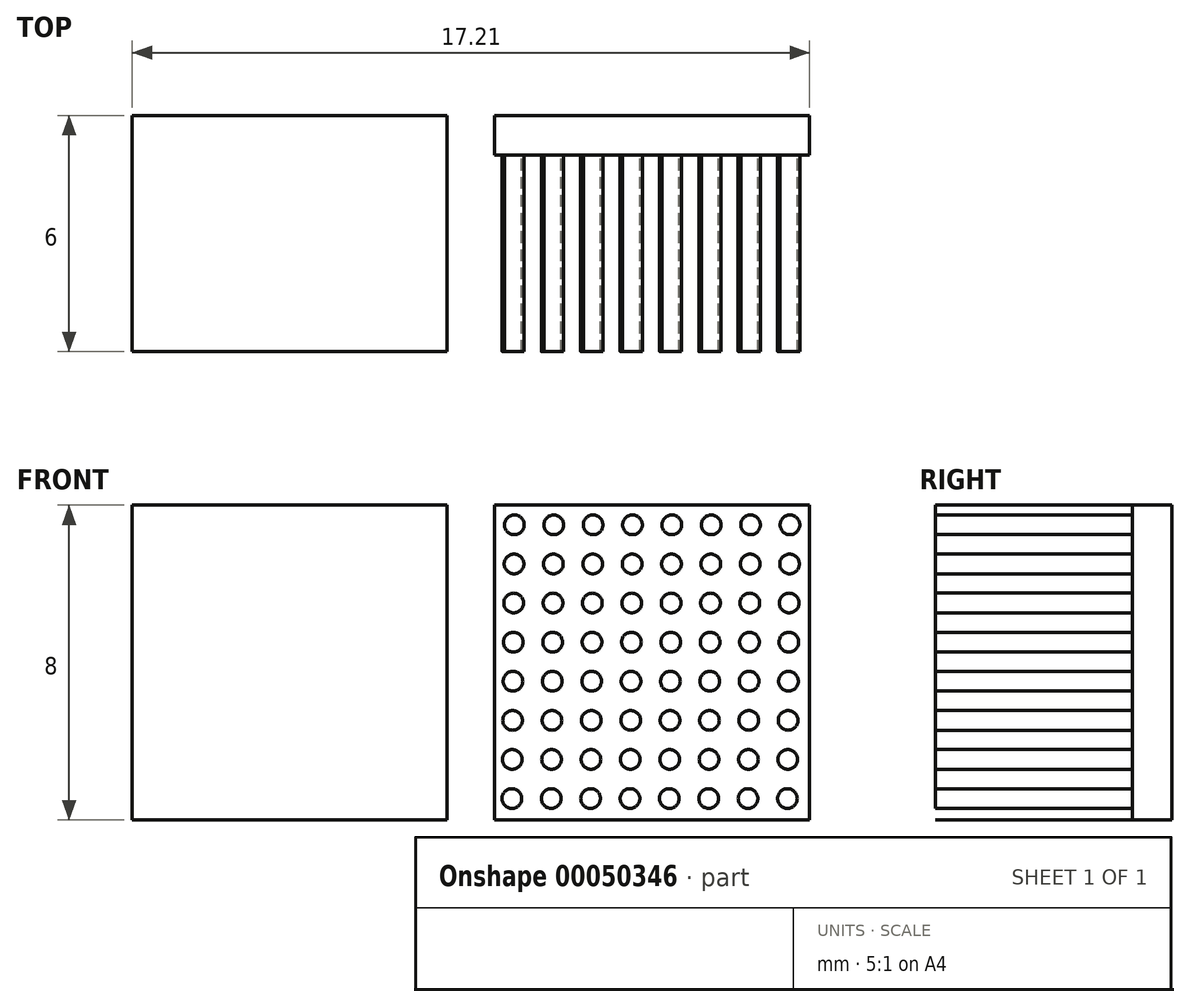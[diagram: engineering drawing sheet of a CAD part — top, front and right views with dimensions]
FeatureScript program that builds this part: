
annotation { "Feature Type Name" : "Feature", "Feature Type Description" : "" }
export const myFeature = defineFeature(function(context is Context, id is Id, definition is map)
    precondition{}
    {
        {
            var Q0;
            Q0=qCreatedBy(makeId("Front.planeOp"),FACE);
            var sketch = newSketch(context, id + "F0", { "sketchPlane" : qUnion([Q0])});
            skLineSegment(sketch, "E0.bottom", {"start": v(0, 0) * mm, "end": v(8, 0) * mm});
            skLineSegment(sketch, "E0.top", {"start": v(0, 8) * mm, "end": v(8, 8) * mm});
            skLineSegment(sketch, "E0.left", {"start": v(0, 0) * mm, "end": v(0, 8) * mm});
            skLineSegment(sketch, "E0.right", {"start": v(8, 0) * mm, "end": v(8, 8) * mm});
            skSolve(sketch);
        }
        {
            var Q0;
            Q0=makeQuery(id+"F0.imprint","IMPRINT",FACE,{"disambiguationData":[TD([[makeQuery(id+"F0.imprint","IMPRINT",EDGE,{"derivedFrom":sQuery(id+"F0.wireOp",EDGE,"E0.bottom")}),1.0]])]});
            extrude(context, id + "F1", {"entities" : qUnion([Q0]), "depth" : 1 * mm});
        }
        {
            var Q0;
            Q0=makeQuery(id+"F1.opExtrude","CAP_FACE",FACE,{"disambiguationData":[OSD([sQuery(id+"F0.wireOp",EDGE,"E0.bottom"),sQuery(id+"F0.wireOp",EDGE,"E0.top"),sQuery(id+"F0.wireOp",EDGE,"E0.left"),sQuery(id+"F0.wireOp",EDGE,"E0.right")])],"isStart":false});
            var sketch = newSketch(context, id + "F2", { "sketchPlane" : qUnion([Q0])});
            skCircle(sketch, "E1", {"center": v(0.5, 7.5) * mm, "radius": 0.25 * mm});
            skCircle(sketch, "E2.1.0.0", {"center": v(1.5, 7.5) * mm, "radius": 0.25 * mm});
            skCircle(sketch, "E2.2.0.0", {"center": v(2.5, 7.5) * mm, "radius": 0.25 * mm});
            skCircle(sketch, "E2.3.0.0", {"center": v(3.5, 7.5) * mm, "radius": 0.25 * mm});
            skCircle(sketch, "E2.4.0.0", {"center": v(4.5, 7.5) * mm, "radius": 0.25 * mm});
            skCircle(sketch, "E2.5.0.0", {"center": v(5.5, 7.5) * mm, "radius": 0.25 * mm});
            skCircle(sketch, "E2.6.0.0", {"center": v(6.5, 7.5) * mm, "radius": 0.25 * mm});
            skCircle(sketch, "E2.7.0.0", {"center": v(7.5, 7.5) * mm, "radius": 0.25 * mm});
            skLineSegment(sketch, "E2.direction1", {"start": v(0.5, 7.5) * mm, "end": v(1.5, 7.5) * mm, "construction": true});
            skCircle(sketch, "E3.1.0.0", {"center": v(0.5, 6.5) * mm, "radius": 0.25 * mm});
            skCircle(sketch, "E3.1.0.1", {"center": v(1.5, 6.5) * mm, "radius": 0.25 * mm});
            skCircle(sketch, "E3.1.0.2", {"center": v(2.5, 6.5) * mm, "radius": 0.25 * mm});
            skCircle(sketch, "E3.1.0.3", {"center": v(3.5, 6.5) * mm, "radius": 0.25 * mm});
            skCircle(sketch, "E3.1.0.4", {"center": v(4.5, 6.5) * mm, "radius": 0.25 * mm});
            skCircle(sketch, "E3.1.0.5", {"center": v(5.5, 6.5) * mm, "radius": 0.25 * mm});
            skCircle(sketch, "E3.1.0.6", {"center": v(6.5, 6.5) * mm, "radius": 0.25 * mm});
            skCircle(sketch, "E3.1.0.7", {"center": v(7.5, 6.5) * mm, "radius": 0.25 * mm});
            skCircle(sketch, "E3.2.0.0", {"center": v(0.48, 5.51) * mm, "radius": 0.25 * mm});
            skCircle(sketch, "E3.2.0.1", {"center": v(1.48, 5.51) * mm, "radius": 0.25 * mm});
            skCircle(sketch, "E3.2.0.2", {"center": v(2.48, 5.51) * mm, "radius": 0.25 * mm});
            skCircle(sketch, "E3.2.0.3", {"center": v(3.48, 5.51) * mm, "radius": 0.25 * mm});
            skCircle(sketch, "E3.2.0.4", {"center": v(4.48, 5.51) * mm, "radius": 0.25 * mm});
            skCircle(sketch, "E3.2.0.5", {"center": v(5.48, 5.51) * mm, "radius": 0.25 * mm});
            skCircle(sketch, "E3.2.0.6", {"center": v(6.48, 5.51) * mm, "radius": 0.25 * mm});
            skCircle(sketch, "E3.2.0.7", {"center": v(7.48, 5.51) * mm, "radius": 0.25 * mm});
            skCircle(sketch, "E3.3.0.0", {"center": v(0.47, 4.52) * mm, "radius": 0.25 * mm});
            skCircle(sketch, "E3.3.0.1", {"center": v(1.47, 4.52) * mm, "radius": 0.25 * mm});
            skCircle(sketch, "E3.3.0.2", {"center": v(2.47, 4.52) * mm, "radius": 0.25 * mm});
            skCircle(sketch, "E3.3.0.3", {"center": v(3.47, 4.52) * mm, "radius": 0.25 * mm});
            skCircle(sketch, "E3.3.0.4", {"center": v(4.47, 4.52) * mm, "radius": 0.25 * mm});
            skCircle(sketch, "E3.3.0.5", {"center": v(5.47, 4.52) * mm, "radius": 0.25 * mm});
            skCircle(sketch, "E3.3.0.6", {"center": v(6.47, 4.52) * mm, "radius": 0.25 * mm});
            skCircle(sketch, "E3.3.0.7", {"center": v(7.47, 4.52) * mm, "radius": 0.25 * mm});
            skCircle(sketch, "E3.4.0.0", {"center": v(0.46, 3.53) * mm, "radius": 0.25 * mm});
            skCircle(sketch, "E3.4.0.1", {"center": v(1.46, 3.53) * mm, "radius": 0.25 * mm});
            skCircle(sketch, "E3.4.0.2", {"center": v(2.46, 3.53) * mm, "radius": 0.25 * mm});
            skCircle(sketch, "E3.4.0.3", {"center": v(3.46, 3.53) * mm, "radius": 0.25 * mm});
            skCircle(sketch, "E3.4.0.4", {"center": v(4.46, 3.53) * mm, "radius": 0.25 * mm});
            skCircle(sketch, "E3.4.0.5", {"center": v(5.46, 3.53) * mm, "radius": 0.25 * mm});
            skCircle(sketch, "E3.4.0.6", {"center": v(6.46, 3.53) * mm, "radius": 0.25 * mm});
            skCircle(sketch, "E3.4.0.7", {"center": v(7.46, 3.53) * mm, "radius": 0.25 * mm});
            skCircle(sketch, "E3.5.0.0", {"center": v(0.45, 2.53) * mm, "radius": 0.25 * mm});
            skCircle(sketch, "E3.5.0.1", {"center": v(1.45, 2.53) * mm, "radius": 0.25 * mm});
            skCircle(sketch, "E3.5.0.2", {"center": v(2.45, 2.53) * mm, "radius": 0.25 * mm});
            skCircle(sketch, "E3.5.0.3", {"center": v(3.45, 2.53) * mm, "radius": 0.25 * mm});
            skCircle(sketch, "E3.5.0.4", {"center": v(4.45, 2.53) * mm, "radius": 0.25 * mm});
            skCircle(sketch, "E3.5.0.5", {"center": v(5.45, 2.53) * mm, "radius": 0.25 * mm});
            skCircle(sketch, "E3.5.0.6", {"center": v(6.45, 2.53) * mm, "radius": 0.25 * mm});
            skCircle(sketch, "E3.5.0.7", {"center": v(7.45, 2.53) * mm, "radius": 0.25 * mm});
            skCircle(sketch, "E3.6.0.0", {"center": v(0.45, 1.54) * mm, "radius": 0.25 * mm});
            skCircle(sketch, "E3.6.0.1", {"center": v(1.45, 1.54) * mm, "radius": 0.25 * mm});
            skCircle(sketch, "E3.6.0.2", {"center": v(2.45, 1.54) * mm, "radius": 0.25 * mm});
            skCircle(sketch, "E3.6.0.3", {"center": v(3.45, 1.54) * mm, "radius": 0.25 * mm});
            skCircle(sketch, "E3.6.0.4", {"center": v(4.45, 1.54) * mm, "radius": 0.25 * mm});
            skCircle(sketch, "E3.6.0.5", {"center": v(5.45, 1.54) * mm, "radius": 0.25 * mm});
            skCircle(sketch, "E3.6.0.6", {"center": v(6.45, 1.54) * mm, "radius": 0.25 * mm});
            skCircle(sketch, "E3.6.0.7", {"center": v(7.45, 1.54) * mm, "radius": 0.25 * mm});
            skCircle(sketch, "E3.7.0.0", {"center": v(0.44, 0.55) * mm, "radius": 0.25 * mm});
            skCircle(sketch, "E3.7.0.1", {"center": v(1.44, 0.55) * mm, "radius": 0.25 * mm});
            skCircle(sketch, "E3.7.0.2", {"center": v(2.44, 0.55) * mm, "radius": 0.25 * mm});
            skCircle(sketch, "E3.7.0.3", {"center": v(3.44, 0.55) * mm, "radius": 0.25 * mm});
            skCircle(sketch, "E3.7.0.4", {"center": v(4.44, 0.55) * mm, "radius": 0.25 * mm});
            skCircle(sketch, "E3.7.0.5", {"center": v(5.44, 0.55) * mm, "radius": 0.25 * mm});
            skCircle(sketch, "E3.7.0.6", {"center": v(6.44, 0.55) * mm, "radius": 0.25 * mm});
            skCircle(sketch, "E3.7.0.7", {"center": v(7.44, 0.55) * mm, "radius": 0.25 * mm});
            skLineSegment(sketch, "E3.direction1", {"start": v(0.5, 7.5) * mm, "end": v(0.5, 6.5) * mm, "construction": true});
            skSolve(sketch);
        }
        {
            var Q0;
            Q0 = qSketchRegion(id + "F2", true);
            extrude(context, id + "F3", {"entities" : qUnion([Q0]), "operationType" : NewBodyOperationType.ADD, "depth" : 5 * mm});
        }
        {
            var Q0;
            Q0=makeQuery(id+"F1.opExtrude","CAP_FACE",FACE,{"disambiguationData":[OSD([sQuery(id+"F0.wireOp",EDGE,"E0.bottom"),sQuery(id+"F0.wireOp",EDGE,"E0.top"),sQuery(id+"F0.wireOp",EDGE,"E0.left"),sQuery(id+"F0.wireOp",EDGE,"E0.right")])],"isStart":true});
            var sketch = newSketch(context, id + "F4", { "sketchPlane" : qUnion([Q0])});
            skLineSegment(sketch, "E4.bottom", {"start": v(1.21, 0) * mm, "end": v(9.21, 0) * mm});
            skLineSegment(sketch, "E4.top", {"start": v(1.21, 8) * mm, "end": v(9.21, 8) * mm});
            skLineSegment(sketch, "E4.left", {"start": v(1.21, 0) * mm, "end": v(1.21, 8) * mm});
            skLineSegment(sketch, "E4.right", {"start": v(9.21, 0) * mm, "end": v(9.21, 8) * mm});
            skSolve(sketch);
        }
        {
            var Q0;
            Q0=makeQuery(id+"F4.imprint","IMPRINT",FACE,{"disambiguationData":[TD([[makeQuery(id+"F4.imprint","IMPRINT",EDGE,{"derivedFrom":sQuery(id+"F4.wireOp",EDGE,"E4.bottom")}),1.0]])]});
            extrude(context, id + "F5", {"entities" : qUnion([Q0]), "oppositeDirection" : true, "depth" : 6 * mm});
        }
    });
